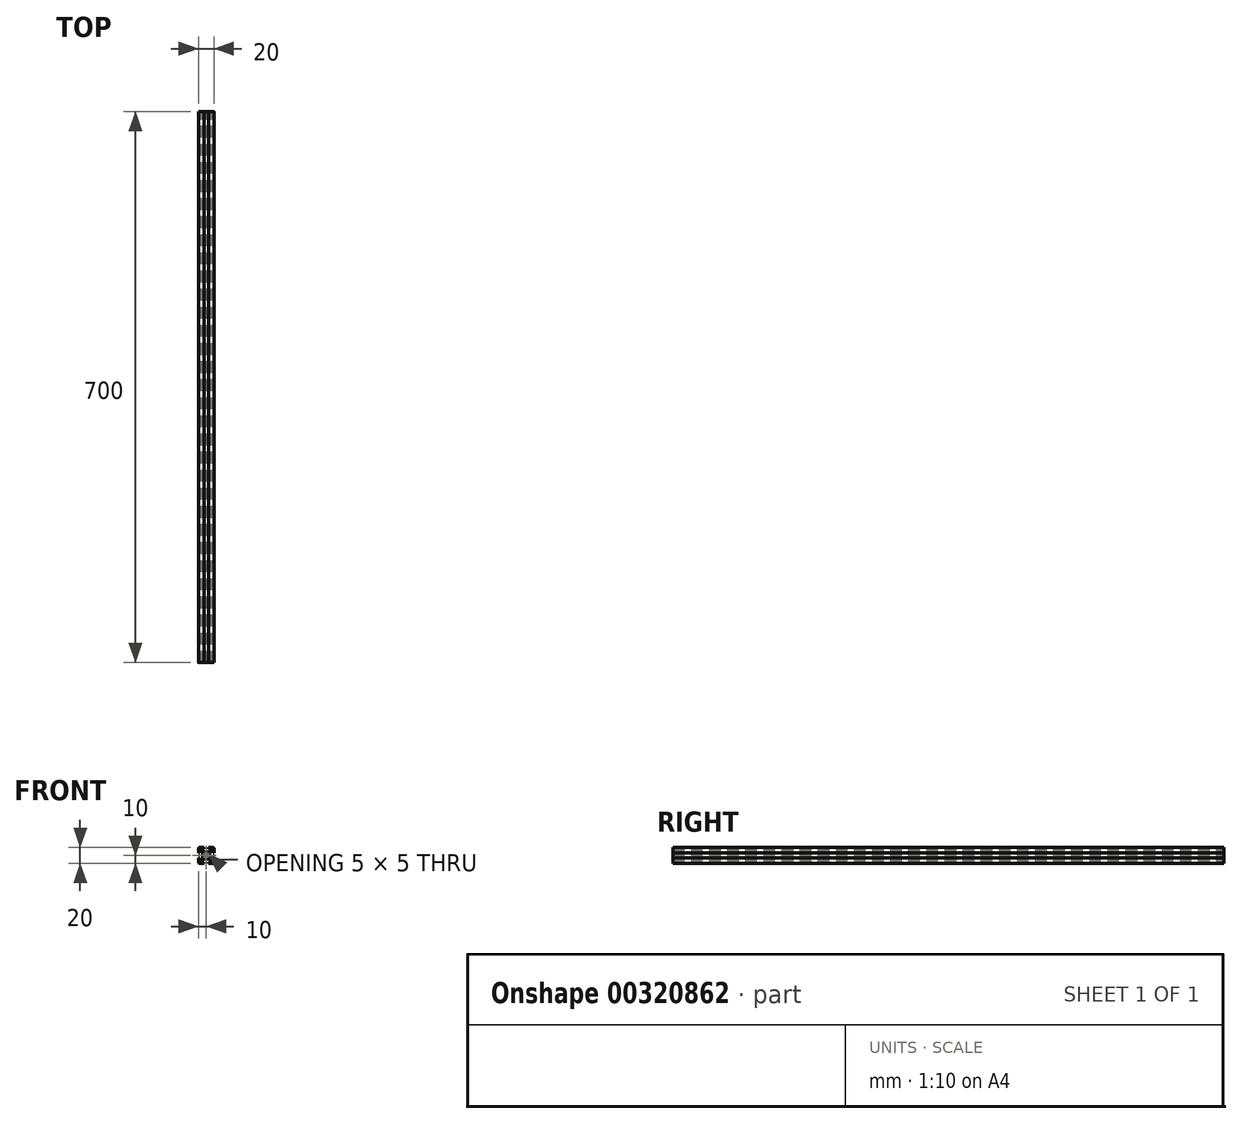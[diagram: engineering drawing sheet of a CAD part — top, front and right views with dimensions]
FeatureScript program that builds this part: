
annotation { "Feature Type Name" : "Feature", "Feature Type Description" : "" }
export const myFeature = defineFeature(function(context is Context, id is Id, definition is map)
    precondition{}
    {
        {
            var Q0;
            Q0=qCreatedBy(makeId("Front.planeOp"),FACE);
            var sketch = newSketch(context, id + "F0", { "sketchPlane" : qUnion([Q0])});
            skLineSegment(sketch, "E0.bottom", {"start": v(8.5, -10) * mm, "end": v(3, -10) * mm});
            skLineSegment(sketch, "E0.top", {"start": v(8.5, 10) * mm, "end": v(3, 10) * mm});
            skLineSegment(sketch, "E0.left", {"start": v(10, -8.5) * mm, "end": v(10, -3) * mm});
            skLineSegment(sketch, "E0.right", {"start": v(-10, -8.5) * mm, "end": v(-10, -3) * mm});
            skPoint(sketch, "E0.middle", {"position": v(0, 0) * mm});
            skLineSegment(sketch, "E1.bottom", {"start": v(6, -8.5) * mm, "end": v(3, -8.5) * mm});
            skLineSegment(sketch, "E1.top", {"start": v(6, 8.5) * mm, "end": v(3, 8.5) * mm});
            skLineSegment(sketch, "E1.left", {"start": v(8.5, -6) * mm, "end": v(8.5, -3) * mm});
            skLineSegment(sketch, "E1.right", {"start": v(-8.5, -6) * mm, "end": v(-8.5, -3) * mm});
            skLineSegment(sketch, "E2.bottom", {"start": v(3.44, -4.5) * mm, "end": v(-3.44, -4.5) * mm});
            skLineSegment(sketch, "E2.top", {"start": v(3.44, 4.5) * mm, "end": v(-3.44, 4.5) * mm});
            skLineSegment(sketch, "E2.left", {"start": v(4.5, -3.44) * mm, "end": v(4.5, 3.44) * mm});
            skLineSegment(sketch, "E2.right", {"start": v(-4.5, -3.44) * mm, "end": v(-4.5, 3.44) * mm});
            skLineSegment(sketch, "E3.bottom", {"start": v(8.5, -6) * mm, "end": v(7.06, -6) * mm});
            skLineSegment(sketch, "E3.top", {"start": v(8.5, 6) * mm, "end": v(7.06, 6) * mm});
            skLineSegment(sketch, "E4.left", {"start": v(6, -8.5) * mm, "end": v(6, -7.06) * mm});
            skLineSegment(sketch, "E4.right", {"start": v(-6, -8.5) * mm, "end": v(-6, -7.06) * mm});
            skPoint(sketch, "E5.orphan", {"position": v(-8.5, 8.5) * mm});
            skPoint(sketch, "E6.orphan", {"position": v(8.5, 8.5) * mm});
            skPoint(sketch, "E7.orphan", {"position": v(8.5, -8.5) * mm});
            skPoint(sketch, "E8.orphan", {"position": v(-8.5, -8.5) * mm});
            skLineSegment(sketch, "E9.trimOffspring", {"start": v(-6, 7.06) * mm, "end": v(-6, 8.5) * mm});
            skLineSegment(sketch, "E10.trimOffspring", {"start": v(-7.06, 6) * mm, "end": v(-8.5, 6) * mm});
            skLineSegment(sketch, "E11.trimOffspring", {"start": v(6, 7.06) * mm, "end": v(6, 8.5) * mm});
            skLineSegment(sketch, "E12.trimOffspring", {"start": v(-7.06, -6) * mm, "end": v(-8.5, -6) * mm});
            skLineSegment(sketch, "E13", {"start": v(-10, 10) * mm, "end": v(0, 0) * mm, "construction": true});
            skLineSegment(sketch, "E14", {"start": v(10, 10) * mm, "end": v(0, 0) * mm, "construction": true});
            skLineSegment(sketch, "E15", {"start": v(-6, 7.06) * mm, "end": v(-3.44, 4.5) * mm});
            skPoint(sketch, "E15.endSnap0", {"position": v(7.25, -6) * mm});
            skLineSegment(sketch, "E16", {"start": v(6, -7.06) * mm, "end": v(3.44, -4.5) * mm});
            skLineSegment(sketch, "E17", {"start": v(7.06, 6) * mm, "end": v(4.5, 3.44) * mm});
            skLineSegment(sketch, "E18", {"start": v(6, 7.06) * mm, "end": v(3.44, 4.5) * mm});
            skPoint(sketch, "E19.orphan", {"position": v(6, -6) * mm});
            skPoint(sketch, "E20.orphan", {"position": v(-4.5, -4.5) * mm});
            skPoint(sketch, "E21.orphan", {"position": v(-4.5, 4.5) * mm});
            skPoint(sketch, "E22.orphan", {"position": v(4.5, 4.5) * mm});
            skPoint(sketch, "E23.orphan", {"position": v(4.5, -4.5) * mm});
            skLineSegment(sketch, "E24.trimOffspring", {"start": v(4.5, -3.44) * mm, "end": v(7.06, -6) * mm});
            skLineSegment(sketch, "E25.trimOffspring", {"start": v(-3.44, -4.5) * mm, "end": v(-6, -7.06) * mm});
            skLineSegment(sketch, "E26.trimOffspring", {"start": v(-4.5, -3.44) * mm, "end": v(-7.06, -6) * mm});
            skLineSegment(sketch, "E27.trimOffspring", {"start": v(-4.5, 3.44) * mm, "end": v(-7.06, 6) * mm});
            skLineSegment(sketch, "E28.bottom", {"start": v(8.5, -3) * mm, "end": v(10, -3) * mm});
            skLineSegment(sketch, "E28.top", {"start": v(8.5, 3) * mm, "end": v(10, 3) * mm});
            skPoint(sketch, "E28.middle", {"position": v(10, 0) * mm});
            skLineSegment(sketch, "E29.left", {"start": v(3, 8.5) * mm, "end": v(3, 10) * mm});
            skLineSegment(sketch, "E29.right", {"start": v(-3, 8.5) * mm, "end": v(-3, 10) * mm});
            skPoint(sketch, "E29.middle", {"position": v(0, 10) * mm});
            skLineSegment(sketch, "E30.bottom", {"start": v(-8.5, 3) * mm, "end": v(-10, 3) * mm});
            skLineSegment(sketch, "E30.top", {"start": v(-8.5, -3) * mm, "end": v(-10, -3) * mm});
            skPoint(sketch, "E30.middle", {"position": v(-10, 0) * mm});
            skLineSegment(sketch, "E31.left", {"start": v(3, -8.5) * mm, "end": v(3, -10) * mm});
            skLineSegment(sketch, "E31.right", {"start": v(-3, -8.5) * mm, "end": v(-3, -10) * mm});
            skPoint(sketch, "E31.middle", {"position": v(0, -10) * mm});
            skPoint(sketch, "E32.orphan", {"position": v(3, 11.5) * mm});
            skPoint(sketch, "E33.orphan", {"position": v(-3, 11.5) * mm});
            skLineSegment(sketch, "E34.trimOffspring", {"start": v(-3, 10) * mm, "end": v(-8.5, 10) * mm});
            skLineSegment(sketch, "E35.trimOffspring", {"start": v(-3, 8.5) * mm, "end": v(-6, 8.5) * mm});
            skPoint(sketch, "E28.right.end.orphan", {"position": v(11.5, 3) * mm});
            skPoint(sketch, "E36.orphan", {"position": v(11.5, -3) * mm});
            skLineSegment(sketch, "E37.trimOffspring", {"start": v(10, 3) * mm, "end": v(10, 8.5) * mm});
            skLineSegment(sketch, "E38.trimOffspring", {"start": v(8.5, 3) * mm, "end": v(8.5, 6) * mm});
            skPoint(sketch, "E39.orphan", {"position": v(3, -11.5) * mm});
            skPoint(sketch, "E40.orphan", {"position": v(-3, -11.5) * mm});
            skLineSegment(sketch, "E41.trimOffspring", {"start": v(-3, -10) * mm, "end": v(-8.5, -10) * mm});
            skLineSegment(sketch, "E42.trimOffspring", {"start": v(-3, -8.5) * mm, "end": v(-6, -8.5) * mm});
            skPoint(sketch, "E30.right.end.orphan", {"position": v(-11.5, -3) * mm});
            skPoint(sketch, "E43.orphan", {"position": v(-11.5, 3) * mm});
            skLineSegment(sketch, "E44.trimOffspring", {"start": v(-10, 3) * mm, "end": v(-10, 8.5) * mm});
            skLineSegment(sketch, "E45.trimOffspring", {"start": v(-8.5, 3) * mm, "end": v(-8.5, 6) * mm});
            skLineSegment(sketch, "E46.trimOffspring", {"start": v(0, 0) * mm, "end": v(10, -10) * mm, "construction": true});
            skLineSegment(sketch, "E47.trimOffspring", {"start": v(0, 0) * mm, "end": v(-10, -10) * mm, "construction": true});
            skArc(sketch, "E48", {"start": v(1.16, 2.22) * mm, "mid": v(0, 2.5) * mm, "end": v(-1.16, 2.22) * mm});
            skLineSegment(sketch, "E49", {"start": v(-2.5, -1.44) * mm, "end": v(1.44, 2.5) * mm});
            skLineSegment(sketch, "E50", {"start": v(2.5, 1.44) * mm, "end": v(-1.44, -2.5) * mm});
            skLineSegment(sketch, "E51", {"start": v(1.44, -2.5) * mm, "end": v(-2.5, 1.44) * mm});
            skLineSegment(sketch, "E52", {"start": v(-1.44, 2.5) * mm, "end": v(2.5, -1.44) * mm});
            skLineSegment(sketch, "E53", {"start": v(2.5, 1.44) * mm, "end": v(2.5, -1.44) * mm, "construction": true});
            skLineSegment(sketch, "E54", {"start": v(1.44, -2.5) * mm, "end": v(-1.44, -2.5) * mm, "construction": true});
            skLineSegment(sketch, "E55", {"start": v(-2.5, -1.44) * mm, "end": v(-2.5, 1.44) * mm, "construction": true});
            skLineSegment(sketch, "E56", {"start": v(-1.44, 2.5) * mm, "end": v(1.44, 2.5) * mm, "construction": true});
            skLineSegment(sketch, "E57", {"start": v(-1.44, 2.5) * mm, "end": v(-2.5, 1.44) * mm});
            skLineSegment(sketch, "E58", {"start": v(1.44, 2.5) * mm, "end": v(2.5, 1.44) * mm});
            skLineSegment(sketch, "E59", {"start": v(2.5, -1.44) * mm, "end": v(1.44, -2.5) * mm});
            skLineSegment(sketch, "E60", {"start": v(-1.44, -2.5) * mm, "end": v(-2.5, -1.44) * mm});
            skArc(sketch, "E61.trimOffspring", {"start": v(-2.22, 1.16) * mm, "mid": v(-2.5, 0) * mm, "end": v(-2.22, -1.16) * mm});
            skArc(sketch, "E62.trimOffspring", {"start": v(-1.16, -2.22) * mm, "mid": v(0, -2.5) * mm, "end": v(1.16, -2.22) * mm});
            skArc(sketch, "E63.trimOffspring", {"start": v(2.22, -1.16) * mm, "mid": v(2.5, 0) * mm, "end": v(2.22, 1.16) * mm});
            skPoint(sketch, "E64.visualSharp", {"position": v(10, 10) * mm});
            skArc(sketch, "E64.filletArc", {"start": v(10, 8.5) * mm, "mid": v(9.56, 9.56) * mm, "end": v(8.5, 10) * mm});
            skPoint(sketch, "E65.visualSharp", {"position": v(10, -10) * mm});
            skArc(sketch, "E65.filletArc", {"start": v(8.5, -10) * mm, "mid": v(9.56, -9.56) * mm, "end": v(10, -8.5) * mm});
            skPoint(sketch, "E66.visualSharp", {"position": v(-10, -10) * mm});
            skArc(sketch, "E66.filletArc", {"start": v(-10, -8.5) * mm, "mid": v(-9.56, -9.56) * mm, "end": v(-8.5, -10) * mm});
            skPoint(sketch, "E67.visualSharp", {"position": v(-10, 10) * mm});
            skArc(sketch, "E67.filletArc", {"start": v(-8.5, 10) * mm, "mid": v(-9.56, 9.56) * mm, "end": v(-10, 8.5) * mm});
            skSolve(sketch);
        }
        {
            assignVariable(context, id + "F2", {"name" : "Length", "anyValue" : 700});
        }
        {
            var Q0;
            Q0=qSketchRegion(id+"F0",true);
            extrude(context, id + "F1", {"entities" : qUnion([Q0]), "depth" : (getVariable(context, 'Length')) * mm});
        }
    });
